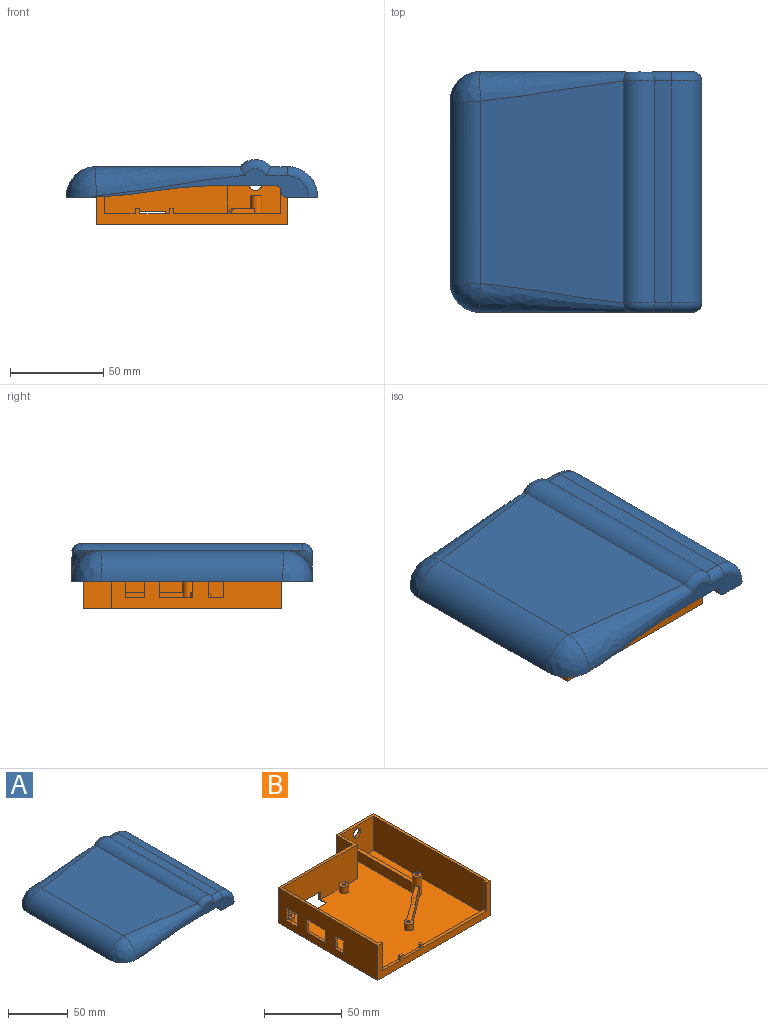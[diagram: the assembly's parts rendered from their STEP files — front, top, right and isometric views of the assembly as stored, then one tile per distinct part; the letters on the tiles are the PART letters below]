
ASSEMBLY  parts=2 mates=1
PART A: 41 faces, bbox 138.1x130.8x24.9 mm
  f0: plane 129x25.54mm, normal (0,0,-1), area 2177mm2, adj f1,f5,f6,f10,f11,f14,f19,f24
  f1: plane 20.89x11.43mm, normal (0,1,0), area 207.1mm2, adj f0,f19,f21,f32,f33
  f2: plane 89.41x15mm, normal (0,-1,0), area 458.3mm2, adj f4,f9,f12,f18,f20,f38
  f3: plane 77.95x11.56mm, normal (0,1,0), area 460.3mm2, adj f4,f18,f20,f29,f30
  f4: plane 126.78x94mm, normal (0,0,-1), area 1310.6mm2, adj f2,f3,f13,f18,f28,f29,f38
  f5: plane 115.55x16.53mm, normal (0,-1,0), area 455.4mm2, adj f0,f24,f25,f26,f27,f28,f34,f35
  f6: plane 102x15mm, normal (0,1,0), area 1098.7mm2, adj f0,f7,f11,f12,f34,f35,f36,f37
  f7: plane 91x14.8mm, normal (1,0,0), area 1347.1mm2, adj f6,f8,f12,f38
  f8: plane 68.09x14.8mm, normal (0,-1,0), area 700.7mm2, adj f7,f9,f12,f38
  f9: plane 15x2.52mm, normal (1,0,0), area 37.8mm2, adj f2,f8,f12,f38
  f10: plane 15x11.67mm, normal (0,-1,0), area 141mm2, adj f0,f11,f12,f19,f21
  f11: plane 106x15mm, normal (-1,0,0), area 1590mm2, adj f0,f6,f10,f12
  f12: plane 106x102mm, normal (0,0,-1), area 9731.1mm2, adj f2,f6,f7,f8,f9,f10,f11,f20
  f13: cylinder r=16.43mm len=97.66mm, axis (0,1,0), area 2517.5mm2, adj f4,f17,f28,f29
  f14: cylinder r=16.43mm len=119mm, axis (0,1,0), area 3071.9mm2, adj f0,f15,f24,f33
  f15: plane 119x8.82mm, normal (0,0,1), area 1049.9mm2, adj f14,f16,f25,f32
  f16: cylinder r=11.06mm len=119mm, axis (0,1,0), area 2229.9mm2, adj f15,f17,f26,f31
  f17: plane 120.82x78.47mm, normal (0,0,1), area 8288.4mm2, adj f13,f16,f27,f30
  f18: plane 9.12x6.5mm, normal (1,0,0), area 59.3mm2, adj f2,f3,f4,f20
  f19: plane 9.12x6.5mm, normal (-1,0,0), area 59.3mm2, adj f0,f1,f10,f21
  f20: cylinder r=8mm len=12mm, axis (0,1,0), area 72.3mm2, adj f2,f3,f12,f18,f22,f23,f30,f31
  f21: cylinder r=8mm len=12mm, axis (0,1,0), area 72.2mm2, adj f1,f10,f12,f19,f22,f23,f31,f32
  f22: plane 10.84x1.43mm, normal (0,1,0), area 12.8mm2, adj f12,f20,f21,f23
  f23: plane 13.28x7.91mm, normal (0,0,-1), area 76.1mm2, adj f20,f21,f22,f31
  f24: torus R=11.43mm, axis (0,-1,0), area 180.3mm2, adj f0,f5,f14,f25
  f25: cylinder r=5mm len=11.52mm, axis (-1,0,0), area 79.9mm2, adj f5,f15,f24,f26
  f26: torus R=6.06mm, axis (0,-1,0), area 142.7mm2, adj f5,f16,f25,f27
  f27: bspline ~82.58x15.61mm, area 1275.7mm2, adj f5,f17,f26,f28
  f28: bspline ~18.45x16.46mm, area 404.5mm2, adj f4,f5,f13,f27,f38
  f29: bspline ~18.35x16.46mm, area 406.8mm2, adj f3,f4,f13,f30
  f30: bspline ~82.53x15.74mm, area 1277.8mm2, adj f3,f17,f20,f29,f31
  f31: torus R=6.06mm, axis (0,-1,0), area 107.5mm2, adj f16,f20,f21,f23,f30,f32
  f32: cylinder r=5mm len=10.34mm, axis (-1,0,0), area 75.9mm2, adj f1,f15,f21,f31,f33
  f33: torus R=11.43mm, axis (0,-1,0), area 180.3mm2, adj f0,f1,f14,f32
  f34: plane 16.5x0.25mm, normal (-1,0,0), area 4.1mm2, adj f5,f6,f39,f40
  f35: plane 26.67x16.5mm, normal (0,0,-1), area 440mm2, adj f5,f6,f37,f40
  f36: plane 16.5x3.25mm, normal (0.15,0,-0.99), area 54.2mm2, adj f5,f6,f37,f38
  f37: cylinder r=250mm len=37.82mm, axis (0,1,0), area 626.4mm2, adj f5,f6,f35,f36
  f38: cylinder r=250mm len=122.5mm, axis (0,-1,0), area 2705.7mm2, adj f2,f4,f5,f6,f7,f8,f9,f28
  f39: cylinder r=3mm len=16.5mm, axis (0,-1,0), area 77.8mm2, adj f0,f5,f6,f34
  f40: cylinder r=3mm len=16.5mm, axis (0,1,0), area 77.8mm2, adj f5,f6,f34,f35
PART B: 70 faces, bbox 102x106x27.7 mm
  f0: plane 102x27.7mm, normal (0,-1,0), area 765.1mm2, adj f2,f11,f12,f18,f20,f21,f22,f23
  f1: plane 98x27mm, normal (0,1,0), area 585.7mm2, adj f2,f10,f19,f20,f21,f22,f23,f24
  f2: plane 106x102mm, normal (0,0,1), area 627.5mm2, adj f0,f1,f11,f12,f13,f14,f15,f19
  f3: plane 10x2mm, normal (0,1,0), area 20mm2, adj f11,f24,f41,f68
  f4: plane 10x2mm, normal (0,-1,0), area 20mm2, adj f11,f24,f41,f68
  f5: plane 10x2mm, normal (0,-1,0), area 20mm2, adj f11,f24,f40,f67
  f6: plane 10x2mm, normal (0,1,0), area 20mm2, adj f11,f24,f40,f67
  f7: plane 10x2mm, normal (0,1,0), area 20mm2, adj f11,f24,f39,f66
  f8: plane 10x2mm, normal (0,-1,0), area 20mm2, adj f11,f24,f39,f66
  f9: plane 7.2x7mm, normal (1,0,0), area 17.9mm2, adj f10,f15,f17,f18,f29,f64
  f10: plane 102x98mm, normal (0,0,1), area 8524.3mm2, adj f1,f9,f16,f17,f19,f24,f28,f29
  f11: plane 91x27.7mm, normal (-1,0,0), area 2160.7mm2, adj f0,f2,f3,f4,f5,f6,f7,f8
  f12: plane 106x27.7mm, normal (1,0,0), area 2936.2mm2, adj f0,f2,f13,f18
  f13: plane 33.91x27.7mm, normal (0,1,0), area 900.9mm2, adj f2,f12,f14,f18,f63
  f14: plane 27.7x15mm, normal (-1,0,0), area 415.5mm2, adj f2,f13,f15,f18
  f15: plane 68.09x27.7mm, normal (0,1,0), area 1785.2mm2, adj f2,f9,f11,f14,f16,f18,f64
  f16: plane 7.2x7mm, normal (-1,0,0), area 17.9mm2, adj f10,f15,f17,f18,f29,f64
  f17: plane 14x0.7mm, normal (0,1,0), area 9.8mm2, adj f9,f10,f16,f18
  f18: plane 106x102mm, normal (0,0,-1), area 9692.7mm2, adj f0,f9,f11,f12,f13,f14,f15,f16
  f19: plane 102x27mm, normal (-1,0,0), area 2754mm2, adj f1,f2,f10,f62
  f20: plane 3x2mm, normal (1,0,0), area 6mm2, adj f0,f1,f22,f37
  f21: plane 3x2mm, normal (-1,0,0), area 6mm2, adj f0,f1,f22,f36
  f22: plane 2.55x2mm, normal (0,0,1), area 5.1mm2, adj f0,f1,f20,f21
  f23: plane 22x2mm, normal (1,0,0), area 44mm2, adj f0,f1,f2,f36
  f24: plane 87x27mm, normal (1,0,0), area 1989mm2, adj f1,f2,f3,f4,f5,f6,f7,f8
  f25: plane 3x2mm, normal (1,0,0), area 6mm2, adj f0,f1,f27,f38
  f26: plane 3x2mm, normal (-1,0,0), area 6mm2, adj f0,f1,f27,f37
  f27: plane 2x2mm, normal (0,0,1), area 4mm2, adj f0,f1,f25,f26
  f28: plane 27x15mm, normal (1,0,0), area 405mm2, adj f2,f10,f29,f62
  f29: plane 68.09x27mm, normal (0,-1,0), area 1747.3mm2, adj f2,f9,f10,f16,f24,f28,f64
  f30: plane 27.28x20.43mm, normal (0.6,-0.8,0), area 215.7mm2, adj f10,f32,f55,f56,f59,f65
  f31: plane 27.2x19.72mm, normal (-0.59,0.81,0), area 211.7mm2, adj f10,f32,f55,f56,f59,f65
  f32: plane 12.7x10.12mm, normal (0,0,1), area 38.2mm2, adj f30,f31,f59,f65
  f33: plane 51.32x8mm, normal (1,0,0), area 410.6mm2, adj f10,f35,f59,f62
  f34: plane 51.31x8mm, normal (-1,0,0), area 410.5mm2, adj f10,f35,f59,f62
  f35: plane 51.32x2.68mm, normal (0,0,1), area 136.7mm2, adj f33,f34,f59,f62
  f36: plane 16.2x2mm, normal (0,0,1), area 32.4mm2, adj f0,f1,f21,f23
  f37: plane 16x2mm, normal (0,0,1), area 32mm2, adj f0,f1,f20,f26
  f38: plane 57.52x2mm, normal (0,0,1), area 115mm2, adj f0,f1,f25,f69
  f39: plane 18x2mm, normal (0,0,1), area 36mm2, adj f7,f8,f11,f24
  f40: plane 10x2mm, normal (0,0,1), area 20mm2, adj f5,f6,f11,f24
  f41: plane 8x2mm, normal (0,0,1), area 16mm2, adj f3,f4,f11,f24
  f42: cylinder r=1.2mm len=5mm, axis (0,0,-1), area 37.7mm2, adj f44,f45
  f43: cylinder r=3mm len=6mm, axis (0,0,-1), area 94.2mm2, adj f10,f44
  f44: plane 6x6mm, normal (0,0,1), area 23.8mm2, adj f42,f43
  f45: plane 2.4x2.4mm, normal (0,0,1), area 4.5mm2, adj f42
  f46: cylinder r=1.2mm len=5mm, axis (0,0,-1), area 37.7mm2, adj f48,f49
  f47: cylinder r=3mm len=6mm, axis (0,0,-1), area 94.2mm2, adj f10,f48
  f48: plane 6x6mm, normal (0,0,1), area 23.8mm2, adj f46,f47
  f49: plane 2.4x2.4mm, normal (0,0,1), area 4.5mm2, adj f46
  f50: cylinder r=1.2mm len=5mm, axis (0,0,-1), area 37.7mm2, adj f52,f53
  f51: cylinder r=3mm len=6mm, axis (0,0,-1), area 94.2mm2, adj f10,f52
  f52: plane 6x6mm, normal (0,0,1), area 23.8mm2, adj f50,f51
  f53: plane 2.4x2.4mm, normal (0,0,1), area 4.5mm2, adj f50
  f54: cylinder r=1.2mm len=5mm, axis (0,0,-1), area 37.7mm2, adj f56,f57
  f55: cylinder r=3mm len=6mm, axis (0,0,-1), area 76.5mm2, adj f10,f30,f31,f56
  f56: plane 19.95x16.09mm, normal (0,0,1), area 78.7mm2, adj f30,f31,f54,f55,f65
  f57: plane 2.4x2.4mm, normal (0,0,1), area 4.5mm2, adj f54
  f58: cylinder r=1.2mm len=15mm, axis (0,0,-1), area 113.1mm2, adj f60,f61
  f59: cylinder r=3mm len=15mm, axis (0,0,-1), area 236.6mm2, adj f10,f30,f31,f32,f33,f34,f35,f60
  f60: plane 6x6mm, normal (0,0,1), area 23.8mm2, adj f58,f59
  f61: plane 2.4x2.4mm, normal (0,0,1), area 4.5mm2, adj f58
  f62: plane 29.91x27mm, normal (0,-1,0), area 747.8mm2, adj f2,f10,f19,f28,f33,f34,f35,f63
  f63: cylinder r=3.5mm len=7mm, axis (0,-1,0), area 44mm2, adj f13,f62
  f64: plane 14x2mm, normal (0,0,-1), area 28mm2, adj f9,f15,f16,f29
  f65: cone r=3mm half-angle=45deg, axis (0,0,1), area 13mm2, adj f30,f31,f32,f56
  f66: plane 18x2mm, normal (0,0,-1), area 36mm2, adj f7,f8,f11,f24
  f67: plane 10x2mm, normal (0,0,-1), area 20mm2, adj f5,f6,f11,f24
  f68: plane 8x2mm, normal (0,0,-1), area 16mm2, adj f3,f4,f11,f24
  f69: plane 22x2mm, normal (-1,0,0), area 44mm2, adj f0,f1,f2,f38
PLACE A t=(-22.76,-52.03,56.33)mm
PLACE B t=(-22.76,-52.03,54.4)mm
MATE slider A.f12 <-> B.f2  axis (0,0,-1) through (29.3,-44.53,83.33)mm
